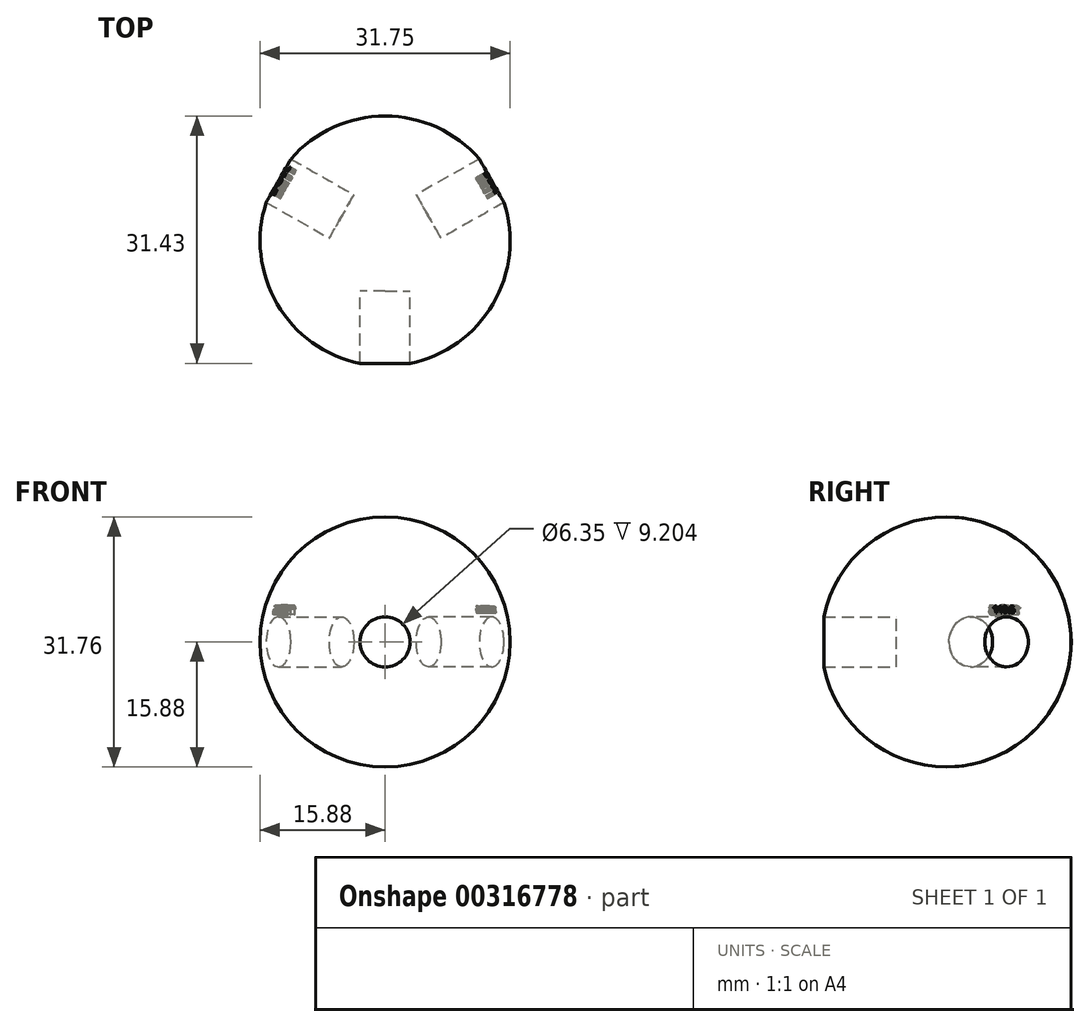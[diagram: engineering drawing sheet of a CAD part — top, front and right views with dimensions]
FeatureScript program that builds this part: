
annotation { "Feature Type Name" : "Feature", "Feature Type Description" : "" }
export const myFeature = defineFeature(function(context is Context, id is Id, definition is map)
    precondition{}
    {
        {
            var Q0;
            Q0=qCreatedBy(makeId("Front.planeOp"),FACE);
            var sketch = newSketch(context, id + "F0", { "sketchPlane" : qUnion([Q0])});
            skArc(sketch, "E0", {"start": v(0, 15.88) * mm, "mid": v(-15.88, 0) * mm, "end": v(0, -15.88) * mm});
            skLineSegment(sketch, "E1", {"start": v(0, 15.88) * mm, "end": v(0, -15.88) * mm});
            skSolve(sketch);
        }
        {
            var Q0;
            Q0=qCreatedBy(makeId("Top.planeOp"),FACE);
            var sketch = newSketch(context, id + "F1", { "sketchPlane" : qUnion([Q0])});
            skCircle(sketch, "E2", {"center": v(0, 0) * mm, "radius": 15.88 * mm});
            skSolve(sketch);
        }
        {
            var Q0;
            Q0=makeQuery(id+"F0.imprint","IMPRINT",FACE,{"disambiguationData":[TD([[makeQuery(id+"F0.imprint","IMPRINT",EDGE,{"derivedFrom":sQuery(id+"F0.wireOp",EDGE,"E0")}),1.0]])]});
            var Q1;
            Q1=sQuery(id+"F1.wireOp",EDGE,"E2");
            revolve(context, id + "F2", {"entities" : qUnion([Q0]), "axis" : qUnion([Q1]), "revolveType" : RevolveType.FULL});
        }
        {
            var Q0;
            Q0=qCreatedBy(makeId("Front.planeOp"),FACE);
            cPlane(context, id + "F3", {"entities" : qUnion([Q0]), "cplaneType" : CPlaneType.OFFSET, "offset" : 6.35 * mm, "width" : 152.4 * mm, "height" : 152.4 * mm});
        }
        {
            var Q0;
            Q0=qCreatedBy(id+"F3.planeOp",FACE);
            var sketch = newSketch(context, id + "F4", { "sketchPlane" : qUnion([Q0])});
            skCircle(sketch, "E3", {"center": v(0, 0) * mm, "radius": 3.18 * mm});
            skSolve(sketch);
        }
        {
            var Q0;
            Q0=qSketchRegion(id+"F4",true);
            extrude(context, id + "F5", {"entities" : qUnion([Q0]), "depth" : 25.4 * mm});
        }
        {
            var Q0;
            Q0=qCreatedBy(makeId("Right.planeOp"),FACE);
            var sketch = newSketch(context, id + "F6", { "sketchPlane" : qUnion([Q0])});
            skLineSegment(sketch, "E4", {"start": v(0, 67.47) * mm, "end": v(0, -53.83) * mm, "construction": true});
            skSolve(sketch);
        }
        {
            var Q0;
            Q0=qCreatedBy(makeId("Top.planeOp"),FACE);
            var sketch = newSketch(context, id + "F7", { "sketchPlane" : qUnion([Q0])});
            skLineSegment(sketch, "E5", {"start": v(69.95, 0) * mm, "end": v(-61.3, 0) * mm, "construction": true});
            skSolve(sketch);
        }
        {
            var Q0;
            Q0=makeQuery(id+"F5.opExtrude","SWEPT_BODY",BODY,{"disambiguationData":[OSD([sQuery(id+"F4.wireOp",EDGE,"E3")])]});
            var Q1;
            Q1=sQuery(id+"F7.wireOp",EDGE,"E5");
            transform(context, id + "F8", {"entities" : qUnion([Q0]), "transformType" : TransformType.ROTATION, "transformAxis" : qUnion([Q1]), "angle" : 119.9 * degree, "makeCopy" : true});
        }
        {
            var Q0;
            Q0=makeQuery(id+"F5.opExtrude","SWEPT_BODY",BODY,{"disambiguationData":[OSD([sQuery(id+"F4.wireOp",EDGE,"E3")])]});
            var Q1;
            Q1=sQuery(id+"F6.wireOp",EDGE,"E4");
            transform(context, id + "F9", {"entities" : qUnion([Q0]), "transformType" : TransformType.ROTATION, "transformAxis" : qUnion([Q1]), "angle" : 119.5 * degree, "makeCopy" : true});
        }
        {
            var Q0;
            Q0=makeQuery(id+"F5.opExtrude","SWEPT_BODY",BODY,{"disambiguationData":[OSD([sQuery(id+"F4.wireOp",EDGE,"E3")])]});
            var Q1;
            Q1=sQuery(id+"F6.wireOp",EDGE,"E4");
            transform(context, id + "F10", {"entities" : qUnion([Q0]), "transformType" : TransformType.ROTATION, "transformAxis" : qUnion([Q1]), "angle" : 119.5 * degree, "oppositeDirection" : true, "makeCopy" : true});
        }
        {
            var Q0;
            Q0=makeQuery(id+"F9.opPattern","COPY",FACE,{"derivedFrom":makeQuery(id+"F5.opExtrude","CAP_FACE",FACE,{"disambiguationData":[OSD([sQuery(id+"F4.wireOp",EDGE,"E3")])],"isStart":false}),"instanceName":"1"});
            cPlane(context, id + "F11", {"entities" : qUnion([Q0]), "cplaneType" : CPlaneType.OFFSET, "offset" : 14.4 * mm, "oppositeDirection" : true, "width" : 152.4 * mm, "height" : 152.4 * mm});
        }
        {
            var Q0;
            Q0=qCreatedBy(id+"F11.planeOp",FACE);
            var sketch = newSketch(context, id + "F12", { "sketchPlane" : qUnion([Q0])});
            skText(sketch, "E6", { "text": "119.5", "fontName": "OpenSans-Bold.ttf"});
            const initialGuessF12  = {"E6": [-0.00236, 0.00346, 1, 0, 0.00121]};
            skSetInitialGuess(sketch, initialGuessF12);
            skSolve(sketch);
        }
        {
            var Q0;
            Q0 = qSketchRegion(id + "F12", true);
            extrude(context, id + "F13", {"entities" : qUnion([Q0]), "operationType" : NewBodyOperationType.REMOVE, "oppositeDirection" : true, "depth" : 3.1 * mm});
        }
        {
            var Q0;
            Q0=makeQuery(id+"F10.opPattern","COPY",FACE,{"derivedFrom":makeQuery(id+"F5.opExtrude","CAP_FACE",FACE,{"disambiguationData":[OSD([sQuery(id+"F4.wireOp",EDGE,"E3")])],"isStart":false}),"instanceName":"1"});
            cPlane(context, id + "F14", {"entities" : qUnion([Q0]), "cplaneType" : CPlaneType.OFFSET, "offset" : 15.06 * mm, "oppositeDirection" : true, "width" : 152.4 * mm, "height" : 152.4 * mm});
        }
        {
            var Q0;
            Q0=qCreatedBy(id+"F14.planeOp",FACE);
            var sketch = newSketch(context, id + "F15", { "sketchPlane" : qUnion([Q0])});
            skText(sketch, "E7", { "text": "119.5", "fontName": "OpenSans-Bold.ttf"});
            const initialGuessF15  = {"E7": [-0.00178, 0.0037, 1, 0, 0.00088]};
            skSetInitialGuess(sketch, initialGuessF15);
            skSolve(sketch);
        }
        {
            var Q0;
            Q0 = qSketchRegion(id + "F15", true);
            extrude(context, id + "F16", {"entities" : qUnion([Q0]), "operationType" : NewBodyOperationType.REMOVE, "oppositeDirection" : true, "depth" : 2.72 * mm});
        }
        {
            var Q0;
            Q0=makeQuery(id+"F5.opExtrude","SWEPT_BODY",BODY,{"disambiguationData":[OSD([sQuery(id+"F4.wireOp",EDGE,"E3")])]});
            var Q1;
            Q1=makeQuery(id+"F2.opRevolve","SWEPT_BODY",BODY,{"disambiguationData":[OSD([sQuery(id+"F0.wireOp",EDGE,"E0"),sQuery(id+"F0.wireOp",EDGE,"E1")])]});
            booleanBodies(context, id + "F17", {"operationType" : BooleanOperationType.SUBTRACTION, "tools" : qUnion([Q0]), "targets" : qUnion([Q1])});
        }
        {
            var Q0;
            Q0=makeQuery(id+"F9.opPattern","COPY",BODY,{"derivedFrom":makeQuery(id+"F5.opExtrude","SWEPT_BODY",BODY,{"disambiguationData":[OSD([sQuery(id+"F4.wireOp",EDGE,"E3")])]}),"instanceName":"1"});
            var Q1;
            Q1=makeQuery(id+"F2.opRevolve","SWEPT_BODY",BODY,{"disambiguationData":[OSD([sQuery(id+"F0.wireOp",EDGE,"E0"),sQuery(id+"F0.wireOp",EDGE,"E1")])]});
            booleanBodies(context, id + "F18", {"operationType" : BooleanOperationType.SUBTRACTION, "tools" : qUnion([Q0]), "targets" : qUnion([Q1])});
        }
        {
            var Q0;
            Q0=makeQuery(id+"F10.opPattern","COPY",BODY,{"derivedFrom":makeQuery(id+"F5.opExtrude","SWEPT_BODY",BODY,{"disambiguationData":[OSD([sQuery(id+"F4.wireOp",EDGE,"E3")])]}),"instanceName":"1"});
            var Q1;
            Q1=makeQuery(id+"F2.opRevolve","SWEPT_BODY",BODY,{"disambiguationData":[OSD([sQuery(id+"F0.wireOp",EDGE,"E0"),sQuery(id+"F0.wireOp",EDGE,"E1")])]});
            booleanBodies(context, id + "F19", {"operationType" : BooleanOperationType.SUBTRACTION, "tools" : qUnion([Q0]), "targets" : qUnion([Q1])});
        }
        {
            var Q0;
            Q0=makeQuery(id+"F8.opPattern","COPY",BODY,{"derivedFrom":makeQuery(id+"F5.opExtrude","SWEPT_BODY",BODY,{"disambiguationData":[OSD([sQuery(id+"F4.wireOp",EDGE,"E3")])]}),"instanceName":"1"});
            deleteBodies(context, id + "F20", {"entities" : qUnion([Q0])});
        }
    });
